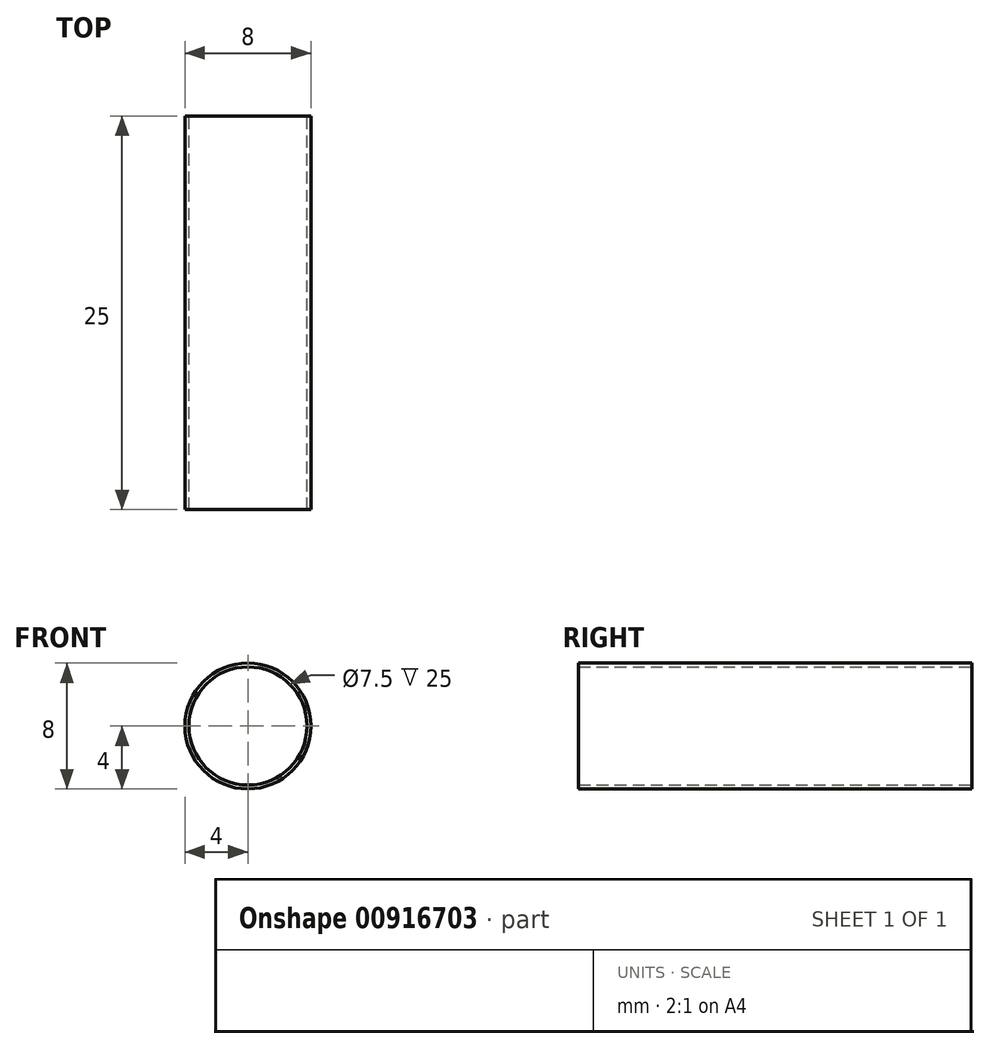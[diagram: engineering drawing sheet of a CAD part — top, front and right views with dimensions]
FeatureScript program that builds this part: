
annotation { "Feature Type Name" : "Feature", "Feature Type Description" : "" }
export const myFeature = defineFeature(function(context is Context, id is Id, definition is map)
    precondition{}
    {
        {
            var Q0;
            Q0=qCreatedBy(makeId("Front.planeOp"),FACE);
            var sketch = newSketch(context, id + "F0", { "sketchPlane" : qUnion([Q0])});
            skCircle(sketch, "E0", {"center": v(0, 0) * mm, "radius": 4 * mm});
            skCircle(sketch, "E1", {"center": v(0, 0) * mm, "radius": 3.75 * mm});
            skSolve(sketch);
        }
        {
            var Q0;
            Q0=qCreatedBy(makeId("Top.planeOp"),FACE);
            var sketch = newSketch(context, id + "F1", { "sketchPlane" : qUnion([Q0])});
            skLineSegment(sketch, "E2", {"start": v(0, 0) * mm, "end": v(0, 25) * mm});
            skSolve(sketch);
        }
        {
            var Q0;
            Q0 = qSketchRegion(id + "F0", true);
            var Q1;
            Q1 = qConstructionFilter(qBodyType(qCreatedBy(id + "F1" ,EDGE), BodyType.WIRE), ConstructionObject.NO);
            sweep(context, id + "F2", {"profiles" : qUnion([Q0]), "path" : qUnion([Q1])});
        }
    });
